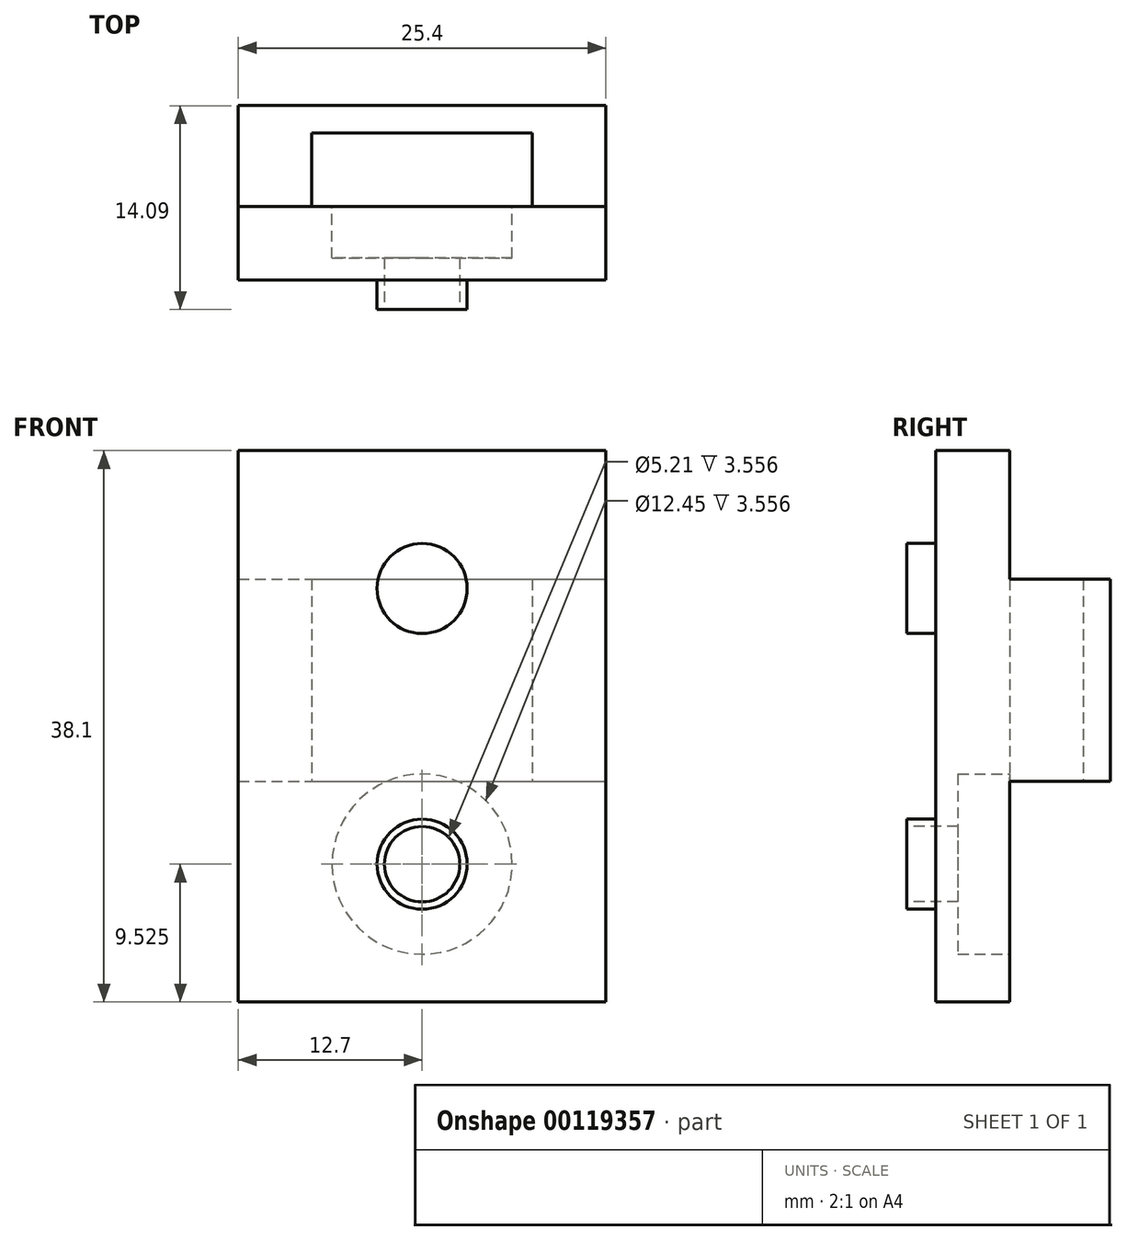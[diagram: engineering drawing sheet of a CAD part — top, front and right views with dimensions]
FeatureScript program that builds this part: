
annotation { "Feature Type Name" : "Feature", "Feature Type Description" : "" }
export const myFeature = defineFeature(function(context is Context, id is Id, definition is map)
    precondition{}
    {
        {
            var Q0;
            Q0=qCreatedBy(makeId("Front.planeOp"),FACE);
            var sketch = newSketch(context, id + "F0", { "sketchPlane" : qUnion([Q0])});
            skCircle(sketch, "E0", {"center": v(0, -9.53) * mm, "radius": 3.11 * mm});
            skCircle(sketch, "E1", {"center": v(0, 9.53) * mm, "radius": 3.11 * mm});
            skLineSegment(sketch, "E2", {"start": v(0, 9.53) * mm, "end": v(0, 0) * mm, "construction": true});
            skLineSegment(sketch, "E3", {"start": v(0, 0) * mm, "end": v(0, -9.53) * mm, "construction": true});
            skSolve(sketch);
        }
        {
            var Q0;
            Q0=qSketchRegion(id+"F0",true);
            extrude(context, id + "F1", {"entities" : qUnion([Q0]), "depth" : 2.03 * mm});
        }
        {
            var Q0;
            Q0=qCreatedBy(makeId("Front.planeOp"),FACE);
            var sketch = newSketch(context, id + "F2", { "sketchPlane" : qUnion([Q0])});
            skLineSegment(sketch, "E4.bottom", {"start": v(-12.7, 19.05) * mm, "end": v(12.7, 19.05) * mm});
            skLineSegment(sketch, "E4.top", {"start": v(-12.7, -19.05) * mm, "end": v(12.7, -19.05) * mm});
            skLineSegment(sketch, "E4.left", {"start": v(-12.7, 19.05) * mm, "end": v(-12.7, -19.05) * mm});
            skLineSegment(sketch, "E4.right", {"start": v(12.7, 19.05) * mm, "end": v(12.7, -19.05) * mm});
            skPoint(sketch, "E4.middle", {"position": v(0, 0) * mm});
            skSolve(sketch);
        }
        {
            var Q0;
            Q0=qSketchRegion(id+"F2",true);
            extrude(context, id + "F3", {"entities" : qUnion([Q0]), "operationType" : NewBodyOperationType.ADD, "oppositeDirection" : true, "depth" : 5.08 * mm});
        }
        {
            var Q0;
            Q0=makeQuery(id+"F1.opExtrude","CAP_FACE",FACE,{"disambiguationData":[OSD([sQuery(id+"F0.wireOp",EDGE,"E0")])],"isStart":false});
            var sketch = newSketch(context, id + "F4", { "sketchPlane" : qUnion([Q0])});
            skCircle(sketch, "E5", {"center": v(0, -9.52) * mm, "radius": 2.6 * mm});
            skSolve(sketch);
        }
        {
            var Q0;
            Q0=qSketchRegion(id+"F4",true);
            extrude(context, id + "F5", {"entities" : qUnion([Q0]), "operationType" : NewBodyOperationType.REMOVE, "endBound" : BoundingType.UP_TO_NEXT, "oppositeDirection" : true, "depth" : 25.4 * mm});
        }
        {
            var Q0;
            Q0=makeQuery(id+"F3.opExtrude","CAP_FACE",FACE,{"disambiguationData":[OSD([sQuery(id+"F2.wireOp",EDGE,"E4.bottom"),sQuery(id+"F2.wireOp",EDGE,"E4.top"),sQuery(id+"F2.wireOp",EDGE,"E4.left"),sQuery(id+"F2.wireOp",EDGE,"E4.right")])],"isStart":false});
            var sketch = newSketch(context, id + "F6", { "sketchPlane" : qUnion([Q0])});
            skCircle(sketch, "E6", {"center": v(0, -9.52) * mm, "radius": 6.22 * mm});
            skSolve(sketch);
        }
        {
            var Q0;
            Q0=qSketchRegion(id+"F6",true);
            extrude(context, id + "F7", {"entities" : qUnion([Q0]), "operationType" : NewBodyOperationType.REMOVE, "oppositeDirection" : true, "depth" : 3.56 * mm});
        }
        {
            var Q0;
            Q0=qCreatedBy(makeId("Top.planeOp"),FACE);
            var sketch = newSketch(context, id + "F8", { "sketchPlane" : qUnion([Q0])});
            skLineSegment(sketch, "E7", {"start": v(12.7, 5.08) * mm, "end": v(12.7, 12.07) * mm});
            skLineSegment(sketch, "E8", {"start": v(12.7, 12.07) * mm, "end": v(-12.7, 12.07) * mm});
            skLineSegment(sketch, "E9", {"start": v(-12.7, 12.07) * mm, "end": v(-12.7, 5.08) * mm});
            skLineSegment(sketch, "E10", {"start": v(-12.7, 5.08) * mm, "end": v(-7.62, 5.08) * mm});
            skLineSegment(sketch, "E11", {"start": v(-7.62, 5.08) * mm, "end": v(-7.62, 10.16) * mm});
            skLineSegment(sketch, "E12", {"start": v(-7.62, 10.16) * mm, "end": v(7.62, 10.16) * mm});
            skLineSegment(sketch, "E13", {"start": v(7.62, 10.16) * mm, "end": v(7.62, 5.08) * mm});
            skLineSegment(sketch, "E14", {"start": v(12.7, 5.08) * mm, "end": v(7.62, 5.08) * mm});
            skLineSegment(sketch, "E15", {"start": v(7.62, 5.08) * mm, "end": v(0, 5.08) * mm, "construction": true});
            skLineSegment(sketch, "E16", {"start": v(0, 5.08) * mm, "end": v(-7.62, 5.08) * mm, "construction": true});
            skSolve(sketch);
        }
        {
            var Q0;
            Q0=qSketchRegion(id+"F8",true);
            var Q1;
            Q1=makeQuery(id+"F3.opExtrude","SWEPT_FACE",FACE,{"disambiguationData":[OSD([sQuery(id+"F2.wireOp",EDGE,"E4.bottom")])]});
            extrude(context, id + "F9", {"entities" : qUnion([Q0]), "operationType" : NewBodyOperationType.ADD, "endBound" : BoundingType.SYMMETRIC, "endBoundEntityFace" : qUnion([Q1]), "depth" : 38.1 * mm});
        }
        {
            var Q0;
            Q0=qCreatedBy(makeId("Right.planeOp"),FACE);
            var sketch = newSketch(context, id + "F10", { "sketchPlane" : qUnion([Q0])});
            skLineSegment(sketch, "E17.bottom", {"start": v(12.07, 19.05) * mm, "end": v(5.08, 19.05) * mm});
            skLineSegment(sketch, "E17.top", {"start": v(12.07, 10.16) * mm, "end": v(5.08, 10.16) * mm});
            skLineSegment(sketch, "E17.left", {"start": v(12.07, 19.05) * mm, "end": v(12.07, 10.16) * mm});
            skLineSegment(sketch, "E17.right", {"start": v(5.08, 19.05) * mm, "end": v(5.08, 10.16) * mm});
            skLineSegment(sketch, "E18.bottom", {"start": v(12.07, -19.05) * mm, "end": v(5.08, -19.05) * mm});
            skLineSegment(sketch, "E18.top", {"start": v(12.07, -3.81) * mm, "end": v(5.08, -3.81) * mm});
            skLineSegment(sketch, "E18.left", {"start": v(12.07, -19.05) * mm, "end": v(12.07, -3.81) * mm});
            skLineSegment(sketch, "E18.right", {"start": v(5.08, -19.05) * mm, "end": v(5.08, -3.81) * mm});
            skSolve(sketch);
        }
        {
            var Q0;
            Q0=qSketchRegion(id+"F10",true);
            extrude(context, id + "F11", {"entities" : qUnion([Q0]), "operationType" : NewBodyOperationType.REMOVE, "endBound" : BoundingType.SYMMETRIC, "oppositeDirection" : true, "depth" : 254 * mm});
        }
    });
